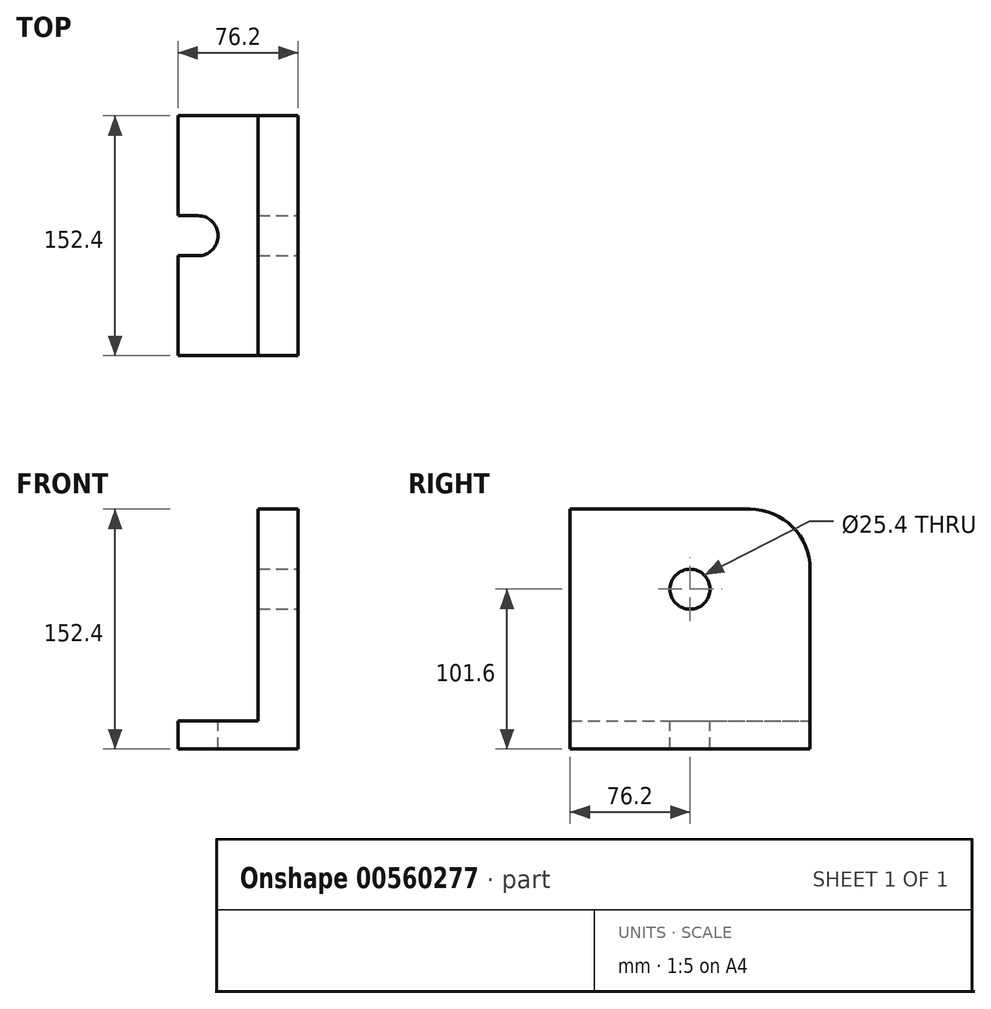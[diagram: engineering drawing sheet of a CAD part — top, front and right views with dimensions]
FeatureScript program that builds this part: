
annotation { "Feature Type Name" : "Feature", "Feature Type Description" : "" }
export const myFeature = defineFeature(function(context is Context, id is Id, definition is map)
    precondition{}
    {
        {
            var Q0;
            Q0=qCreatedBy(makeId("Front.planeOp"),FACE);
            var sketch = newSketch(context, id + "F0", { "sketchPlane" : qUnion([Q0])});
            skLineSegment(sketch, "E0", {"start": v(0, 152.4) * mm, "end": v(-25.4, 152.4) * mm});
            skLineSegment(sketch, "E1", {"start": v(-25.4, 152.4) * mm, "end": v(-25.4, 17.93) * mm});
            skLineSegment(sketch, "E2", {"start": v(-25.4, 17.93) * mm, "end": v(-76.2, 17.93) * mm});
            skLineSegment(sketch, "E3", {"start": v(-76.2, 17.93) * mm, "end": v(-76.2, 0) * mm});
            skLineSegment(sketch, "E4", {"start": v(-76.2, 0) * mm, "end": v(0, 0) * mm});
            skLineSegment(sketch, "E5", {"start": v(0, 0) * mm, "end": v(0, 152.4) * mm});
            skSolve(sketch);
        }
        {
            var Q0;
            Q0=makeQuery(id+"F0.imprint","IMPRINT",FACE,{"disambiguationData":[TD([[makeQuery(id+"F0.imprint","IMPRINT",EDGE,{"derivedFrom":sQuery(id+"F0.wireOp",EDGE,"E0")}),1.0]])]});
            extrude(context, id + "F1", {"entities" : qUnion([Q0]), "endBound" : BoundingType.SYMMETRIC, "depth" : 152.4 * mm, "offsetDistance" : 25.4 * mm});
        }
        {
            var Q0;
            Q0=makeQuery(id+"F1.opExtrude","SWEPT_FACE",FACE,{"disambiguationData":[OSD([sQuery(id+"F0.wireOp",EDGE,"E5")])]});
            var sketch = newSketch(context, id + "F2", { "sketchPlane" : qUnion([Q0])});
            skCircle(sketch, "E6", {"center": v(0, 101.6) * mm, "radius": 12.7 * mm});
            skSolve(sketch);
        }
        {
            var Q0;
            Q0=makeQuery(id+"F2.imprint","IMPRINT",FACE,{"disambiguationData":[TD([[makeQuery(id+"F2.imprint","IMPRINT",EDGE,{"derivedFrom":sQuery(id+"F2.wireOp",EDGE,"E6")}),1.0]])]});
            extrude(context, id + "F3", {"entities" : qUnion([Q0]), "operationType" : NewBodyOperationType.REMOVE, "endBound" : BoundingType.THROUGH_ALL, "oppositeDirection" : true, "depth" : 25.4 * mm, "offsetDistance" : 25.4 * mm});
        }
        {
            var Q0;
            Q0=makeQuery(id+"F1.opExtrude","SWEPT_FACE",FACE,{"disambiguationData":[OSD([sQuery(id+"F0.wireOp",EDGE,"E2")])]});
            var sketch = newSketch(context, id + "F4", { "sketchPlane" : qUnion([Q0])});
            skLineSegment(sketch, "E7", {"start": v(-76.2, 12.7) * mm, "end": v(-63.5, 12.7) * mm});
            skArc(sketch, "E8", {"start": v(-63.5, -12.7) * mm, "mid": v(-50.8, 0) * mm, "end": v(-63.5, 12.7) * mm});
            skLineSegment(sketch, "E9", {"start": v(-76.2, -12.7) * mm, "end": v(-63.5, -12.7) * mm});
            skSolve(sketch);
        }
        {
            var Q0;
            {var subQ0=sQuery(id+"F4.wireOp",EDGE,"E7");Q0=makeQuery(id+"F4.imprint","IMPRINT",FACE,{"disambiguationData":[TD([[makeQuery(id+"F4.imprint","IMPRINT",EDGE,{"derivedFrom":subQ0}),-1.0]])]});}
            extrude(context, id + "F5", {"entities" : qUnion([Q0]), "operationType" : NewBodyOperationType.REMOVE, "endBound" : BoundingType.THROUGH_ALL, "oppositeDirection" : true, "depth" : 25.4 * mm, "offsetDistance" : 25.4 * mm});
        }
        {
            var Q0;
            Q0=makeQuery(id+"F1.opExtrude","SWEPT_FACE",FACE,{"disambiguationData":[OSD([sQuery(id+"F0.wireOp",EDGE,"E1")])]});
            var sketch = newSketch(context, id + "F6", { "sketchPlane" : qUnion([Q0])});
            skArc(sketch, "E10", {"start": v(-38.1, 152.4) * mm, "mid": v(-65.04, 141.24) * mm, "end": v(-76.2, 114.3) * mm});
            skPoint(sketch, "E11", {"position": v(-76.2, 114.3) * mm});
            skPoint(sketch, "E12", {"position": v(-38.1, 152.4) * mm});
            skSolve(sketch);
        }
        {
            var Q0;
            Q0 = qSketchRegion(id + "F6", true);
            var Q1;
            {var subQ0=sQuery(id+"F6.wireOp",EDGE,"E10");Q1=makeQuery(id+"F6.imprint","IMPRINT",FACE,{"disambiguationData":[TD([[makeQuery(id+"F6.imprint","IMPRINT",EDGE,{"derivedFrom":subQ0}),-1.0]])]});}
            extrude(context, id + "F7", {"entities" : qUnion([Q0, Q1]), "operationType" : NewBodyOperationType.REMOVE, "endBound" : BoundingType.THROUGH_ALL, "oppositeDirection" : true, "depth" : 25.4 * mm, "offsetDistance" : 25.4 * mm});
        }
    });
